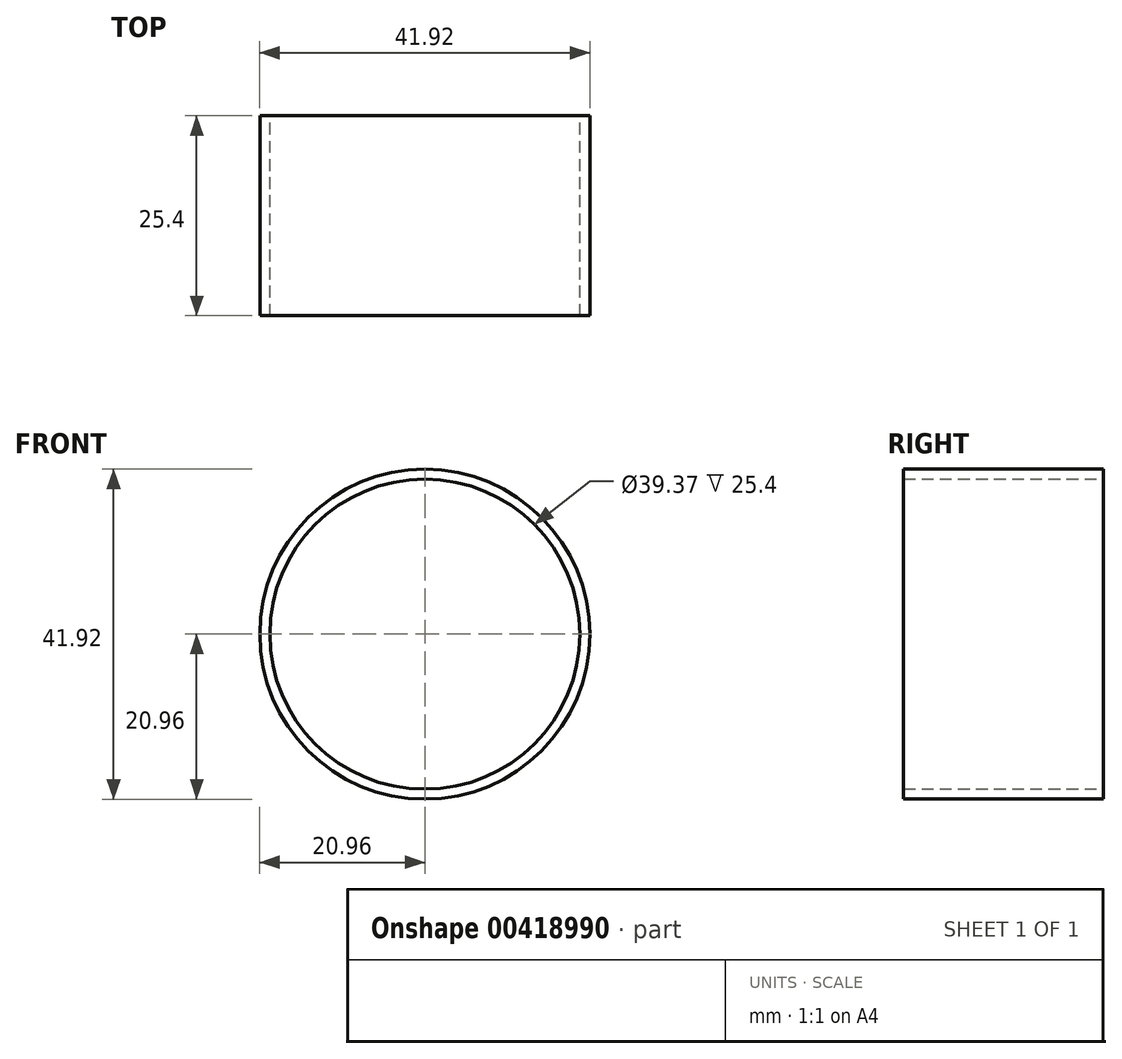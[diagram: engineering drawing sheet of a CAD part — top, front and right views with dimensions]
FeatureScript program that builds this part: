
annotation { "Feature Type Name" : "Feature", "Feature Type Description" : "" }
export const myFeature = defineFeature(function(context is Context, id is Id, definition is map)
    precondition{}
    {
        {
            var Q0;
            Q0=qCreatedBy(makeId("Front.planeOp"),FACE);
            var sketch = newSketch(context, id + "F0", { "sketchPlane" : qUnion([Q0])});
            skCircle(sketch, "E0", {"center": v(0, 0) * mm, "radius": 20.96 * mm});
            skCircle(sketch, "E1", {"center": v(0, 0) * mm, "radius": 19.69 * mm});
            skSolve(sketch);
        }
        {
            var Q0;
            Q0=makeQuery(id+"F0.imprint","IMPRINT",FACE,{"disambiguationData":[TD([[makeQuery(id+"F0.imprint","IMPRINT",EDGE,{"derivedFrom":sQuery(id+"F0.wireOp",EDGE,"E0")}),1.0]])]});
            extrude(context, id + "F1", {"entities" : qUnion([Q0]), "depth" : 25.4 * mm});
        }
    });
